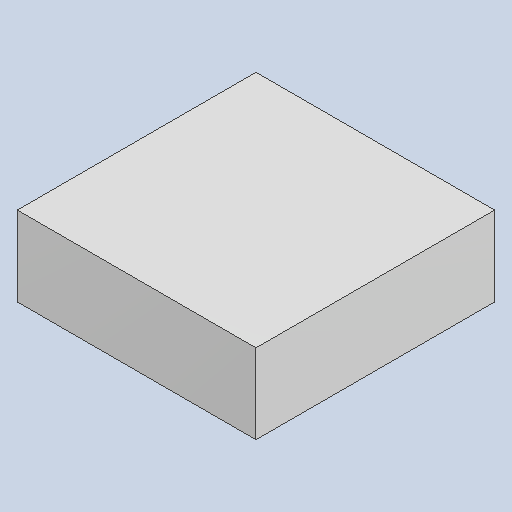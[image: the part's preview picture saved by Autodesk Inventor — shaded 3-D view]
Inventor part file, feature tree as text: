
AUTODESK INVENTOR PART (.ipt)
format: ipt  version: 2023.4 (Build 274418000, 418)  size: 79,872 bytes
history: native  units: mm
features: extrude x1
ambient origin geometry x8: Origin, YZ Plane, XZ Plane, XY Plane, X Axis, Y Axis, Z Axis, Center Point
bodies: Solid1 (feature_tree)
feature tree (1):
  extrude  "Extruded_63"  [1 undecoded]
note: 1 required parameter value undecoded (feature->parameter linkage not recoverable at this tier; creation-order binding heuristic only, values carry confidence <= 0.55)
